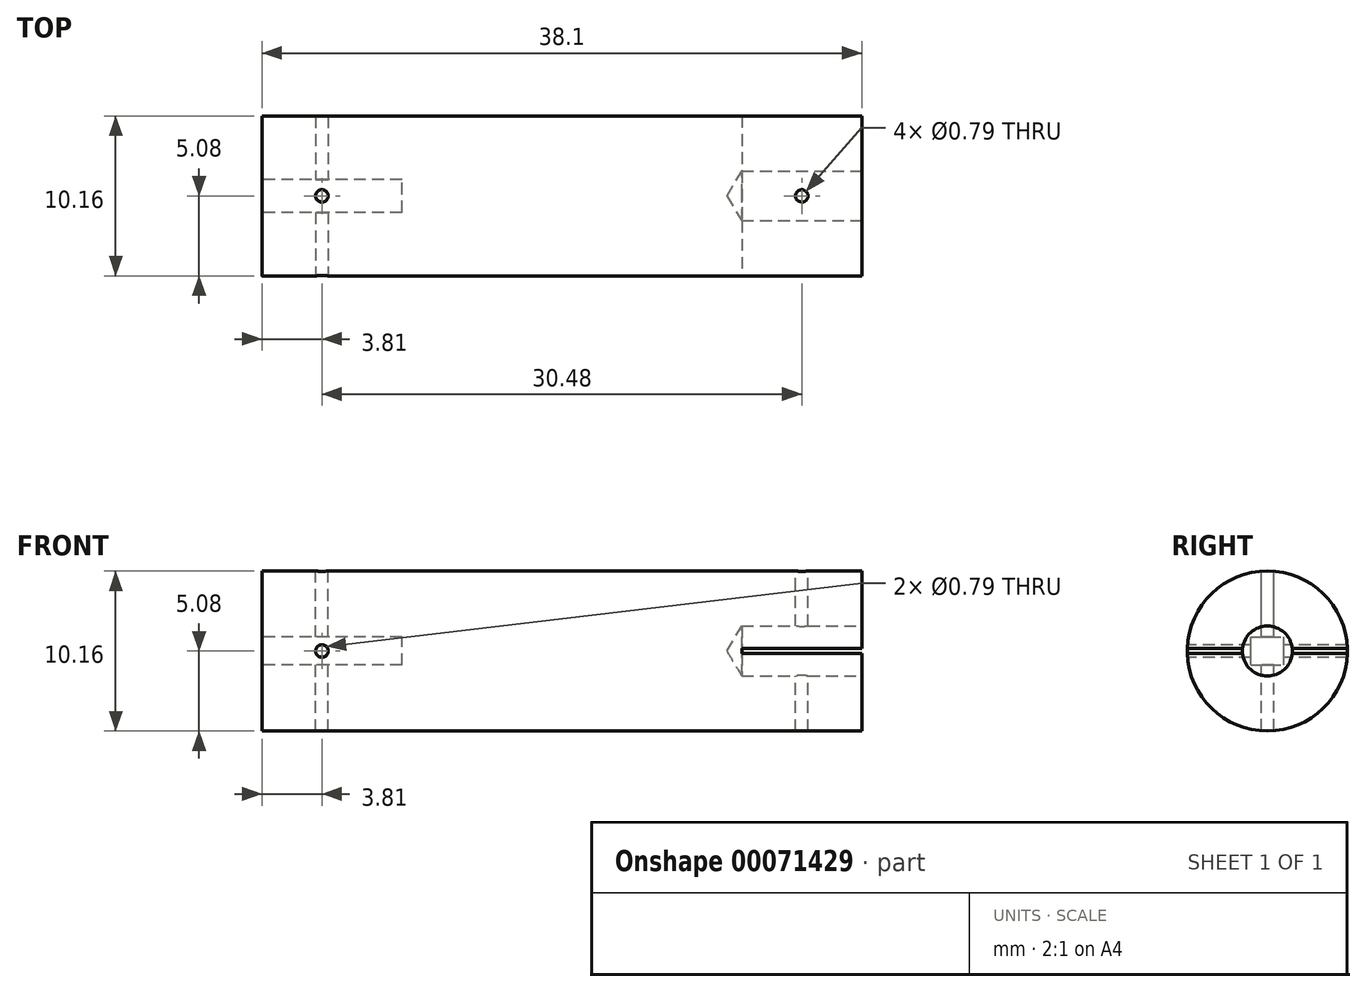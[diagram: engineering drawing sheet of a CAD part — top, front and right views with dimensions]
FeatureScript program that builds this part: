
annotation { "Feature Type Name" : "Feature", "Feature Type Description" : "" }
export const myFeature = defineFeature(function(context is Context, id is Id, definition is map)
    precondition{}
    {
        {
            var Q0;
            Q0=qCreatedBy(makeId("Right.planeOp"),FACE);
            var sketch = newSketch(context, id + "F0", { "sketchPlane" : qUnion([Q0])});
            skCircle(sketch, "E0", {"center": v(0, 0) * mm, "radius": 5.08 * mm});
            skSolve(sketch);
        }
        {
            var Q0;
            Q0 = qSketchRegion(id + "F0", true);
            extrude(context, id + "F1", {"entities" : qUnion([Q0]), "endBound" : BoundingType.SYMMETRIC, "depth" : 38.1 * mm});
        }
        {
            var Q0;
            Q0=makeQuery(id+"F1.opExtrude","CAP_FACE",FACE,{"disambiguationData":[OSD([sQuery(id+"F0.wireOp",EDGE,"E0")])],"isStart":false});
            var sketch = newSketch(context, id + "F2", { "sketchPlane" : qUnion([Q0])});
            skPoint(sketch, "E1", {"position": v(0, 0) * mm});
            skCircle(sketch, "E2", {"center": v(0, 0) * mm, "radius": 1.59 * mm});
            skSolve(sketch);
        }
        {
            var Q0;
            Q0=sQuery(id+"F2.wireOp",VERTEX,"E1");
            var Q1;
            Q1=makeQuery(id+"F1.opExtrude","SWEPT_BODY",BODY,{"disambiguationData":[OSD([sQuery(id+"F0.wireOp",EDGE,"E0")])]});
            hole(context, id + "F3", {"style" : HoleStyle.SIMPLE, "holeDiameter" : 3.17 * mm, "endStyle" : HoleEndStyle.BLIND, "holeDepth" : 7.62 * mm, "locations" : qUnion([Q0]), "scope" : qUnion([Q1])});
        }
        {
            var Q0;
            Q0=makeQuery(id+"F1.opExtrude","CAP_FACE",FACE,{"disambiguationData":[OSD([sQuery(id+"F0.wireOp",EDGE,"E0")])],"isStart":true});
            var sketch = newSketch(context, id + "F4", { "sketchPlane" : qUnion([Q0])});
            skLineSegment(sketch, "E3.rect.bottom", {"start": v(1.05, -0.9) * mm, "end": v(-1.05, -0.9) * mm});
            skLineSegment(sketch, "E3.rect.top", {"start": v(1.05, 0.9) * mm, "end": v(-1.05, 0.9) * mm});
            skLineSegment(sketch, "E3.rect.left", {"start": v(1.05, -0.9) * mm, "end": v(1.05, 0.9) * mm});
            skLineSegment(sketch, "E3.rect.right", {"start": v(-1.05, -0.9) * mm, "end": v(-1.05, 0.9) * mm});
            skPoint(sketch, "E3.rect.middle", {"position": v(0, 0) * mm});
            skSolve(sketch);
        }
        {
            var Q0;
            Q0=makeQuery(id+"F4.imprint","IMPRINT",FACE,{"disambiguationData":[TD([[makeQuery(id+"F4.imprint","IMPRINT",EDGE,{"derivedFrom":sQuery(id+"F4.wireOp",EDGE,"E3.rect.bottom")}),-1.0]])]});
            extrude(context, id + "F5", {"entities" : qUnion([Q0]), "operationType" : NewBodyOperationType.REMOVE, "oppositeDirection" : true, "depth" : 8.9 * mm});
        }
        {
            var Q0;
            Q0=makeQuery(id+"F1.opExtrude","CAP_FACE",FACE,{"disambiguationData":[OSD([sQuery(id+"F0.wireOp",EDGE,"E0")])],"isStart":false});
            var sketch = newSketch(context, id + "F6", { "sketchPlane" : qUnion([Q0])});
            skLineSegment(sketch, "E4.rect.bottom", {"start": v(6.47, 0.16) * mm, "end": v(-6.47, 0.16) * mm});
            skLineSegment(sketch, "E4.rect.top", {"start": v(6.47, -0.16) * mm, "end": v(-6.47, -0.16) * mm});
            skLineSegment(sketch, "E4.rect.left", {"start": v(6.47, 0.16) * mm, "end": v(6.47, -0.16) * mm});
            skLineSegment(sketch, "E4.rect.right", {"start": v(-6.47, 0.16) * mm, "end": v(-6.47, -0.16) * mm});
            skPoint(sketch, "E4.rect.middle", {"position": v(0, 0) * mm});
            skSolve(sketch);
        }
        {
            var Q0;
            {var subQ0=sQuery(id+"F6.wireOp",EDGE,"E4.rect.bottom");var subQ1=makeQuery(id+"F1.opExtrude","CAP_EDGE",EDGE,{"disambiguationData":[OSD([sQuery(id+"F0.wireOp",EDGE,"E0")])],"isStart":false});var subQ2=makeQuery(id+"F6.imprint","INTERSECT",VERTEX,{"disambiguationData":[OD(0.0)],"derivedFrom":[subQ1,subQ0]});Q0=makeQuery(id+"F6.imprint","IMPRINT",FACE,{"disambiguationData":[TD([[makeQuery(id+"F6.imprint","IMPRINT",EDGE,{"disambiguationData":[TD([[subQ2,1.0]])],"derivedFrom":subQ1}),1.0]])]});}
            var Q1;
            {var subQ0=sQuery(id+"F6.wireOp",EDGE,"E4.rect.bottom");var subQ1=makeQuery(id+"F1.opExtrude","CAP_EDGE",EDGE,{"disambiguationData":[OSD([sQuery(id+"F0.wireOp",EDGE,"E0")])],"isStart":false});var subQ2=makeQuery(id+"F6.imprint","INTERSECT",VERTEX,{"disambiguationData":[OD(1.0)],"derivedFrom":[subQ1,subQ0]});Q1=makeQuery(id+"F6.imprint","IMPRINT",FACE,{"disambiguationData":[TD([[makeQuery(id+"F6.imprint","IMPRINT",EDGE,{"disambiguationData":[TD([[subQ2,-1.0]])],"derivedFrom":subQ1}),1.0]])]});}
            extrude(context, id + "F7", {"entities" : qUnion([Q0, Q1]), "operationType" : NewBodyOperationType.REMOVE, "oppositeDirection" : true, "depth" : 7.62 * mm});
        }
        {
            var Q0;
            Q0=qCreatedBy(makeId("Top.planeOp"),FACE);
            cPlane(context, id + "F8", {"entities" : qUnion([Q0]), "cplaneType" : CPlaneType.OFFSET, "offset" : 12.7 * mm, "width" : 152.4 * mm, "height" : 152.4 * mm});
        }
        {
            var Q0;
            Q0=qCreatedBy(id+"F8.planeOp",FACE);
            var sketch = newSketch(context, id + "F9", { "sketchPlane" : qUnion([Q0])});
            skPoint(sketch, "E5", {"position": v(15.24, 0) * mm});
            skCircle(sketch, "E6", {"center": v(15.24, 0) * mm, "radius": 0.4 * mm});
            skPoint(sketch, "E7", {"position": v(-15.24, 0) * mm});
            skCircle(sketch, "E8", {"center": v(-15.24, 0) * mm, "radius": 0.4 * mm});
            skSolve(sketch);
        }
        {
            var Q0;
            Q0=makeQuery(id+"F9.imprint","IMPRINT",FACE,{"disambiguationData":[TD([[makeQuery(id+"F9.imprint","IMPRINT",EDGE,{"derivedFrom":sQuery(id+"F9.wireOp",EDGE,"E8")}),1.0]])]});
            var Q1;
            Q1=makeQuery(id+"F9.imprint","IMPRINT",FACE,{"disambiguationData":[TD([[makeQuery(id+"F9.imprint","IMPRINT",EDGE,{"derivedFrom":sQuery(id+"F9.wireOp",EDGE,"E6")}),1.0]])]});
            extrude(context, id + "F10", {"entities" : qUnion([Q0, Q1]), "operationType" : NewBodyOperationType.REMOVE, "endBound" : BoundingType.THROUGH_ALL, "oppositeDirection" : true, "depth" : 25.4 * mm});
        }
        {
            var Q0;
            Q0=qCreatedBy(makeId("Front.planeOp"),FACE);
            cPlane(context, id + "F11", {"entities" : qUnion([Q0]), "cplaneType" : CPlaneType.OFFSET, "offset" : 12.7 * mm, "width" : 152.4 * mm, "height" : 152.4 * mm});
        }
        {
            var Q0;
            Q0=qCreatedBy(id+"F11.planeOp",FACE);
            var sketch = newSketch(context, id + "F12", { "sketchPlane" : qUnion([Q0])});
            skPoint(sketch, "E9", {"position": v(-15.24, 0) * mm});
            skCircle(sketch, "E10", {"center": v(-15.24, 0) * mm, "radius": 0.4 * mm});
            skSolve(sketch);
        }
        {
            var Q0;
            Q0 = qSketchRegion(id + "F12", true);
            extrude(context, id + "F13", {"entities" : qUnion([Q0]), "operationType" : NewBodyOperationType.REMOVE, "oppositeDirection" : true, "depth" : 25.4 * mm});
        }
    });
